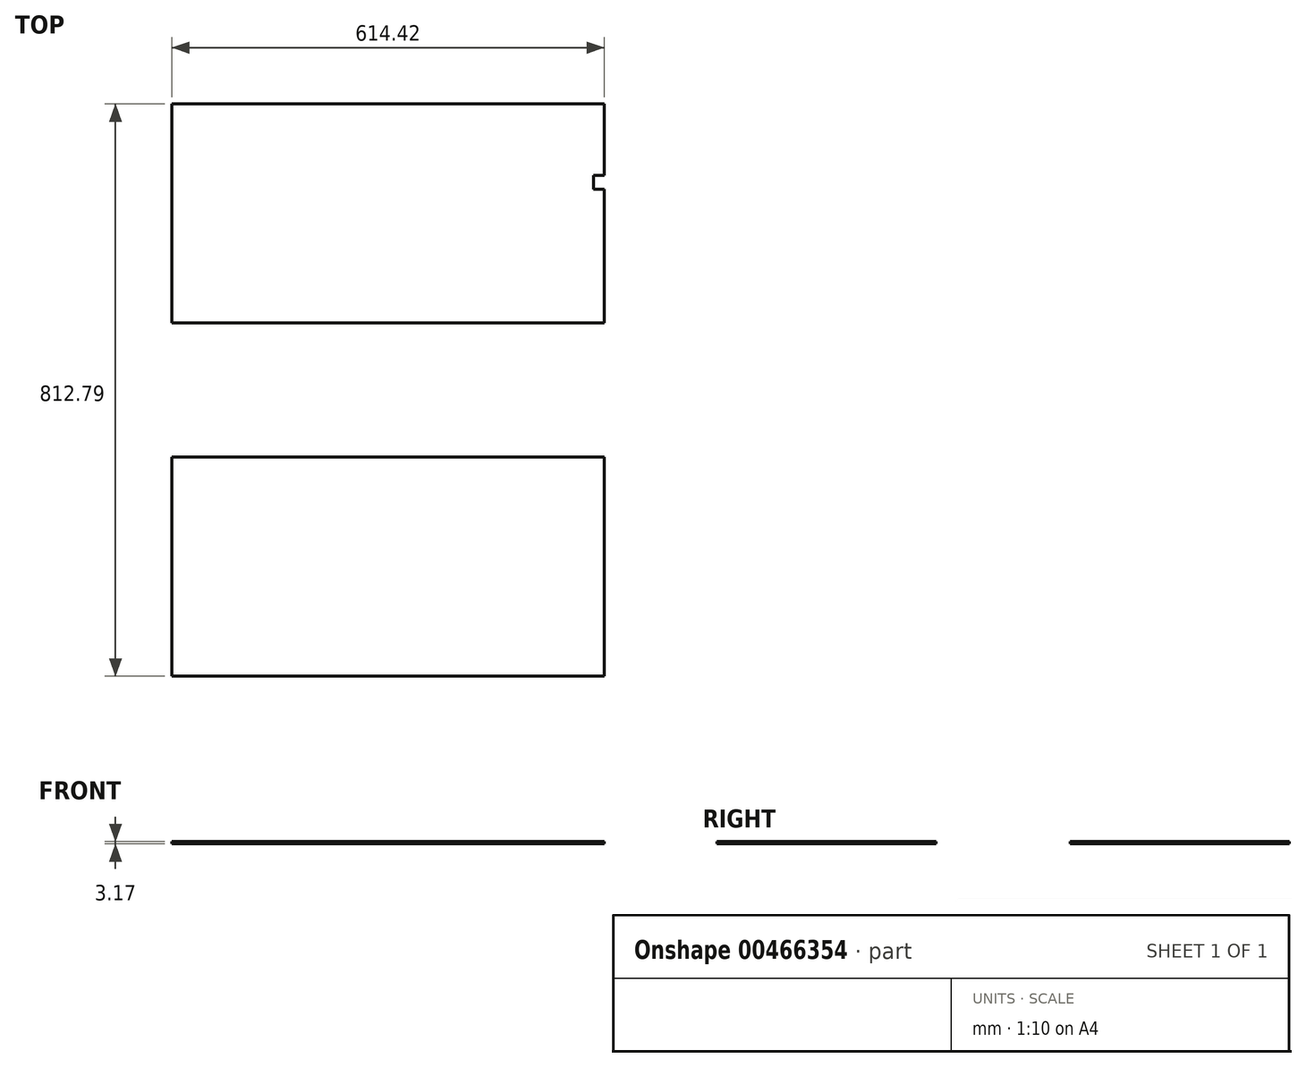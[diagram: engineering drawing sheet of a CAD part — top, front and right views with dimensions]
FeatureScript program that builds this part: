
annotation { "Feature Type Name" : "Feature", "Feature Type Description" : "" }
export const myFeature = defineFeature(function(context is Context, id is Id, definition is map)
    precondition{}
    {
        {
            var Q0;
            Q0=qCreatedBy(makeId("Top.planeOp"),FACE);
            var sketch = newSketch(context, id + "F0", { "sketchPlane" : qUnion([Q0])});
            skLineSegment(sketch, "E0.bottom", {"start": v(307.21, 155.58) * mm, "end": v(-307.21, 155.57) * mm});
            skLineSegment(sketch, "E0.top", {"start": v(307.21, -155.57) * mm, "end": v(-307.21, -155.58) * mm});
            skLineSegment(sketch, "E0.left", {"start": v(307.21, 155.58) * mm, "end": v(307.21, -155.58) * mm});
            skLineSegment(sketch, "E0.right", {"start": v(-307.21, 155.57) * mm, "end": v(-307.21, -155.58) * mm});
            skPoint(sketch, "E0.middle", {"position": v(0, 0) * mm});
            skLineSegment(sketch, "E1.bottom", {"start": v(307.21, -346.07) * mm, "end": v(-307.21, -346.08) * mm});
            skLineSegment(sketch, "E1.top", {"start": v(307.21, -657.22) * mm, "end": v(-307.21, -657.23) * mm});
            skLineSegment(sketch, "E1.left", {"start": v(307.21, -346.07) * mm, "end": v(307.21, -657.22) * mm});
            skLineSegment(sketch, "E1.right", {"start": v(-307.21, -346.08) * mm, "end": v(-307.21, -657.23) * mm});
            skPoint(sketch, "E1.middle", {"position": v(0, -501.65) * mm});
            skLineSegment(sketch, "E2.bottom", {"start": v(142.11, -155.58) * mm, "end": v(-142.11, -155.57) * mm});
            skPoint(sketch, "E2.middle", {"position": v(0, -177.8) * mm});
            skLineSegment(sketch, "E3", {"start": v(-142.11, -346.08) * mm, "end": v(142.11, -346.07) * mm});
            skLineSegment(sketch, "E4", {"start": v(-142.11, -346.08) * mm, "end": v(-142.11, -155.57) * mm});
            skLineSegment(sketch, "E5", {"start": v(142.11, -155.58) * mm, "end": v(142.11, -346.07) * mm});
            skLineSegment(sketch, "E6.bottom", {"start": v(307.21, 53.97) * mm, "end": v(291.97, 53.97) * mm});
            skLineSegment(sketch, "E6.top", {"start": v(307.21, 34.48) * mm, "end": v(291.97, 34.48) * mm});
            skLineSegment(sketch, "E6.left", {"start": v(307.21, 53.97) * mm, "end": v(307.21, 34.48) * mm});
            skLineSegment(sketch, "E6.right", {"start": v(291.97, 53.97) * mm, "end": v(291.97, 34.48) * mm});
            skSolve(sketch);
        }
        {
            var Q0;
            Q0=makeQuery(id+"F0.imprint","IMPRINT",FACE,{"disambiguationData":[TD([[makeQuery(id+"F0.imprint","IMPRINT",EDGE,{"derivedFrom":sQuery(id+"F0.wireOp",EDGE,"E0.bottom")}),1.0]])]});
            var Q1;
            {var subQ5=sQuery(id+"F0.wireOp",EDGE,"E2.bottom");Q1=makeQuery(id+"F0.imprint","IMPRINT",FACE,{"disambiguationData":[TD([[makeQuery(id+"F0.imprint","IMPRINT",EDGE,{"derivedFrom":subQ5}),1.0]])]});}
            var Q2;
            Q2=makeQuery(id+"F0.imprint","IMPRINT",FACE,{"disambiguationData":[TD([[makeQuery(id+"F0.imprint","IMPRINT",EDGE,{"derivedFrom":sQuery(id+"F0.wireOp",EDGE,"E1.top")}),-1.0]])]});
            extrude(context, id + "F1", {"entities" : qUnion([Q0, Q1, Q2]), "depth" : 3.17 * mm});
        }
    });
